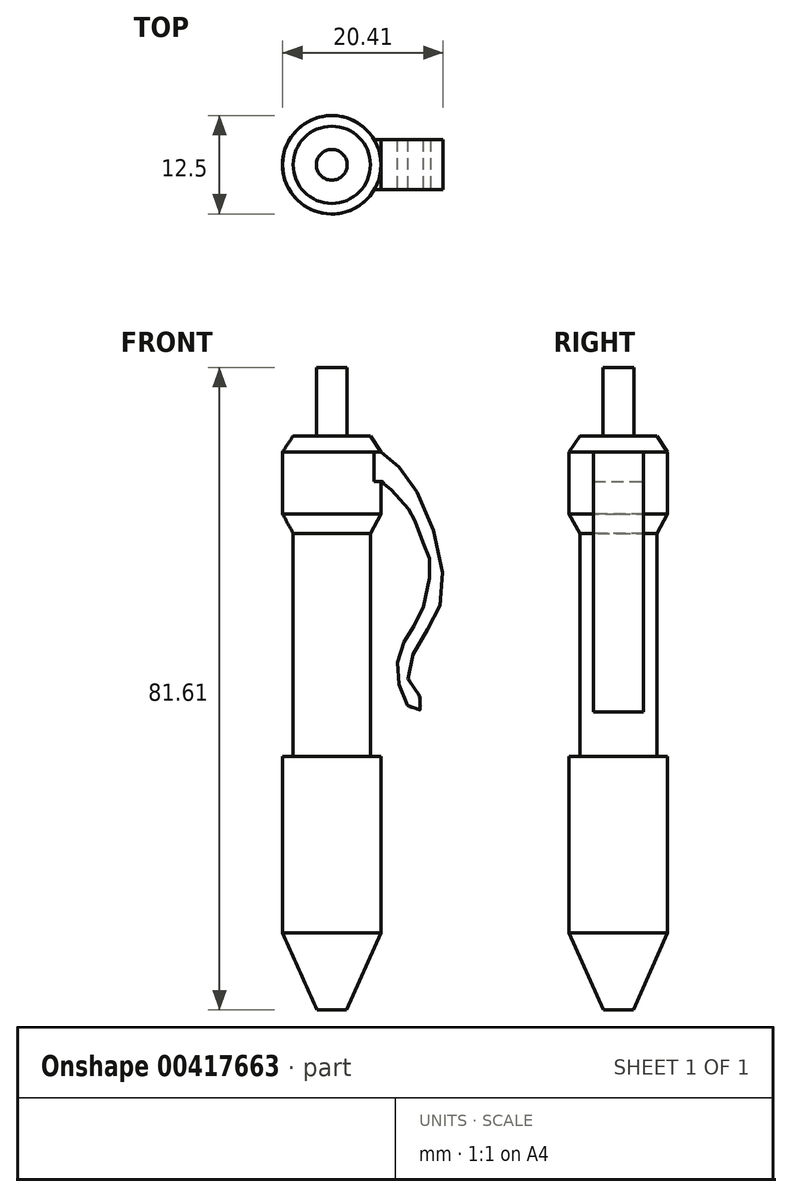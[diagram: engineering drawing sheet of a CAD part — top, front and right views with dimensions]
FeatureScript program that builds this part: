
annotation { "Feature Type Name" : "Feature", "Feature Type Description" : "" }
export const myFeature = defineFeature(function(context is Context, id is Id, definition is map)
    precondition{}
    {
        {
            var Q0;
            Q0=qCreatedBy(makeId("Front.planeOp"),FACE);
            var sketch = newSketch(context, id + "F0", { "sketchPlane" : qUnion([Q0])});
            skLineSegment(sketch, "E0", {"start": v(0, 0) * mm, "end": v(0, 81.61) * mm});
            skLineSegment(sketch, "E1", {"start": v(0, 0) * mm, "end": v(1.89, 0) * mm});
            skLineSegment(sketch, "E2", {"start": v(1.89, 0) * mm, "end": v(6.25, 9.77) * mm});
            skLineSegment(sketch, "E3", {"start": v(6.25, 9.77) * mm, "end": v(6.25, 32.23) * mm});
            skLineSegment(sketch, "E4", {"start": v(6.25, 32.23) * mm, "end": v(4.9, 32.23) * mm});
            skLineSegment(sketch, "E5", {"start": v(4.9, 32.23) * mm, "end": v(4.9, 60.53) * mm});
            skLineSegment(sketch, "E6", {"start": v(4.9, 60.53) * mm, "end": v(6.25, 63) * mm});
            skLineSegment(sketch, "E7", {"start": v(6.25, 63) * mm, "end": v(6.25, 70.9) * mm});
            skLineSegment(sketch, "E8", {"start": v(6.25, 70.9) * mm, "end": v(4.9, 72.9) * mm});
            skLineSegment(sketch, "E9", {"start": v(4.9, 72.9) * mm, "end": v(1.95, 72.9) * mm});
            skLineSegment(sketch, "E10", {"start": v(1.95, 72.9) * mm, "end": v(1.95, 81.61) * mm});
            skLineSegment(sketch, "E11", {"start": v(1.95, 81.61) * mm, "end": v(0, 81.61) * mm});
            skSolve(sketch);
        }
        {
            var Q0;
            Q0=makeQuery(id+"F0.imprint","IMPRINT",FACE,{"disambiguationData":[TD([[makeQuery(id+"F0.imprint","IMPRINT",EDGE,{"derivedFrom":sQuery(id+"F0.wireOp",EDGE,"E0")}),-1.0]])]});
            var Q1;
            Q1=sQuery(id+"F0.wireOp",EDGE,"E0");
            revolve(context, id + "F1", {"entities" : qUnion([Q0]), "axis" : qUnion([Q1]), "revolveType" : RevolveType.FULL});
        }
        {
            var Q0;
            Q0=qCreatedBy(makeId("Front.planeOp"),FACE);
            var sketch = newSketch(context, id + "F2", { "sketchPlane" : qUnion([Q0])});
            skFitSpline(sketch, "E12", {"points": [v(6.25, 70.9) * mm, v(10.3, 66.75) * mm, v(14.13, 53.37) * mm, v(11.46, 47.21) * mm, v(9.74, 41.71) * mm, v(11.61, 38.99) * mm, v(10.65, 37.87) * mm, v(8.94, 40.1) * mm, v(8.38, 44.34) * mm, v(9.74, 47.72) * mm, v(11.46, 50.65) * mm, v(12.52, 56.65) * mm, v(12.01, 58.32) * mm, v(10.5, 62.26) * mm, v(9.84, 63.52) * mm, v(6.66, 66.95) * mm, v(6.26, 67.13) * mm], "startDerivative": vector(52.56, -39.06) * mm, "endDerivative": vector(-14.4, 0.48) * mm});
            skLineSegment(sketch, "E13", {"start": v(6.25, 70.9) * mm, "end": v(5.34, 70.9) * mm});
            skLineSegment(sketch, "E14", {"start": v(5.34, 70.9) * mm, "end": v(5.34, 67.1) * mm});
            skLineSegment(sketch, "E15", {"start": v(5.34, 67.1) * mm, "end": v(6.26, 67.13) * mm});
            skSolve(sketch);
        }
        {
            var Q0;
            Q0 = qSketchRegion(id + "F2", true);
            extrude(context, id + "F3", {"entities" : qUnion([Q0]), "operationType" : NewBodyOperationType.ADD, "endBound" : BoundingType.SYMMETRIC, "depth" : 6.35 * mm});
        }
    });
